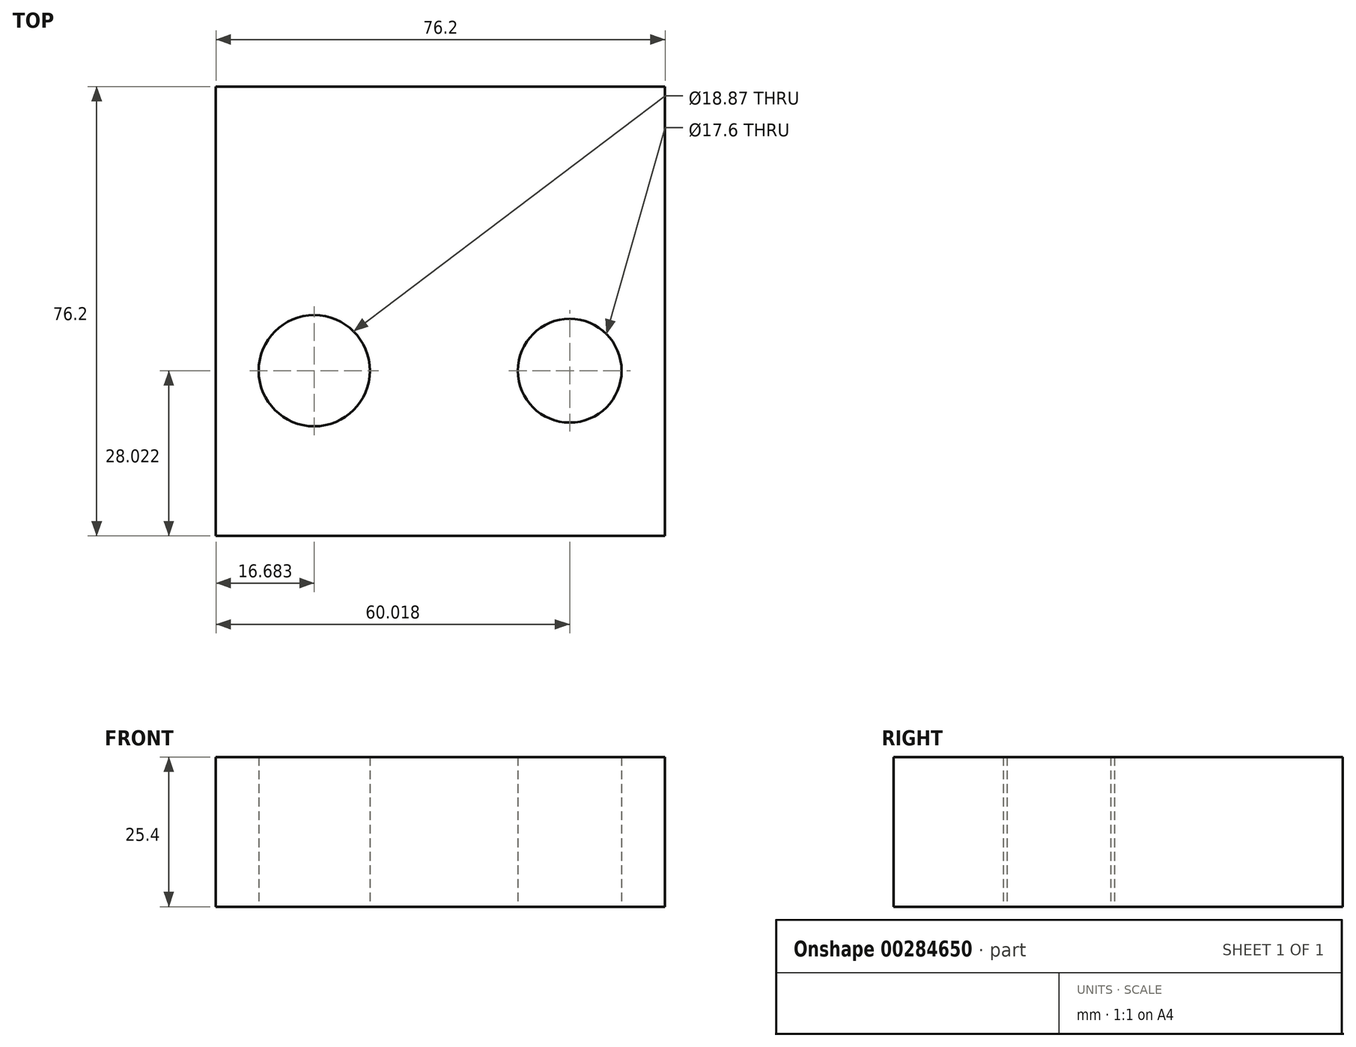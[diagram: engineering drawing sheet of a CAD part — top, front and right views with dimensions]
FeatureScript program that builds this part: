
annotation { "Feature Type Name" : "Feature", "Feature Type Description" : "" }
export const myFeature = defineFeature(function(context is Context, id is Id, definition is map)
    precondition{}
    {
        {
            var Q0;
            Q0=qCreatedBy(makeId("Top.planeOp"),FACE);
            var sketch = newSketch(context, id + "F0", { "sketchPlane" : qUnion([Q0])});
            skLineSegment(sketch, "E0.bottom", {"start": v(-46.44, 42.4) * mm, "end": v(29.76, 42.4) * mm});
            skLineSegment(sketch, "E0.top", {"start": v(-46.44, -33.8) * mm, "end": v(29.76, -33.8) * mm});
            skLineSegment(sketch, "E0.left", {"start": v(-46.44, 42.4) * mm, "end": v(-46.44, -33.8) * mm});
            skLineSegment(sketch, "E0.right", {"start": v(29.76, 42.4) * mm, "end": v(29.76, -33.8) * mm});
            skLineSegment(sketch, "E1", {"start": v(-46.44, 15.02) * mm, "end": v(29.76, 15.02) * mm});
            skCircle(sketch, "E2", {"center": v(13.58, -5.78) * mm, "radius": 8.8 * mm});
            skCircle(sketch, "E3", {"center": v(-29.76, -5.78) * mm, "radius": 9.43 * mm});
            skSolve(sketch);
        }
        {
            var Q0;
            Q0 = qSketchRegion(id + "F0", true);
            extrude(context, id + "F1", {"entities" : qUnion([Q0]), "depth" : 25.4 * mm});
        }
    });
